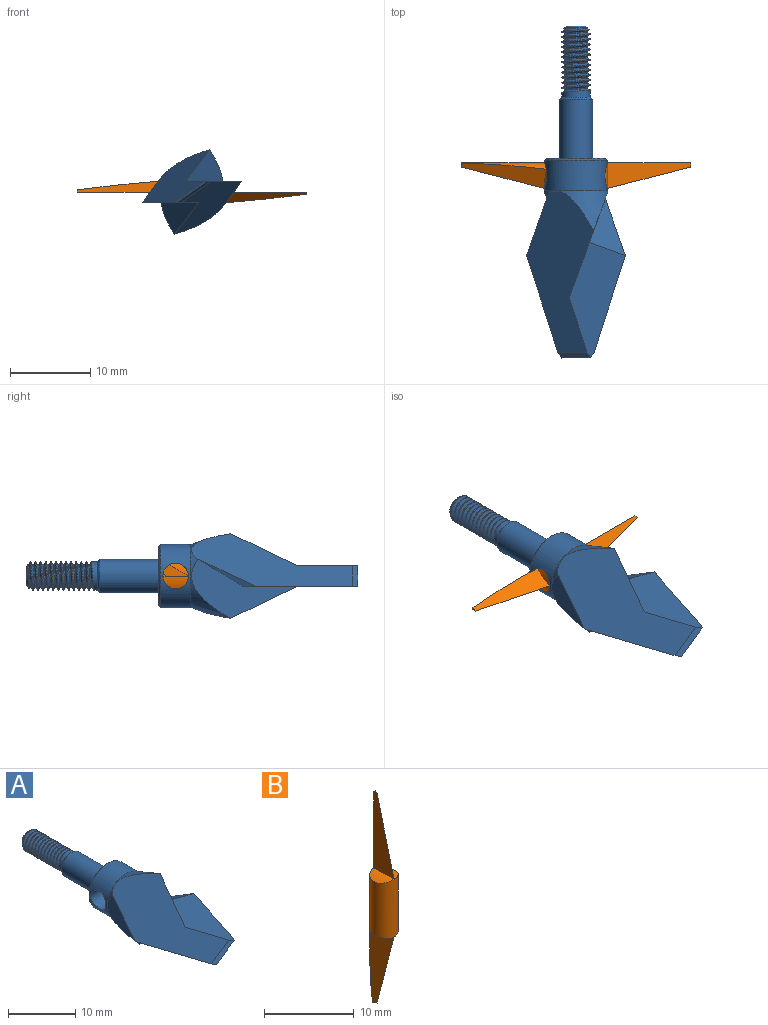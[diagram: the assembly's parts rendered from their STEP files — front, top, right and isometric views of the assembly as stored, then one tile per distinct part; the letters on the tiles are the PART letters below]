
ASSEMBLY  parts=2 mates=1
PART A: 37 faces, bbox 12.7x41.9x11.8 mm
  f0: cylinder r=2.08mm len=7.37mm, axis (0,-1,0), area 96.4mm2, adj f2,f23
  f1: plane 3.66x3.66mm, normal (0,1,0), area 0.9mm2, adj f2,f3
  f2: cone r=2.08mm half-angle=45deg, axis (0,-1,0), area 4.4mm2, adj f0,f1
  f3: cylinder r=1.75mm len=3.51mm, axis (0,-1,0), area 7.4mm2, adj f1,f4,f18,f20,f21
  f4: cylinder r=1.75mm len=3.51mm, axis (0,-1,0), area 1mm2, adj f3,f5,f20,f21
  f5: cylinder r=1.75mm len=3.51mm, axis (0,-1,0), area 1mm2, adj f4,f6,f20,f21
  f6: cylinder r=1.75mm len=3.51mm, axis (0,-1,0), area 1mm2, adj f5,f7,f20,f21
  f7: cylinder r=1.75mm len=3.51mm, axis (0,-1,0), area 1mm2, adj f6,f8,f20,f21
  f8: cylinder r=1.75mm len=3.51mm, axis (0,-1,0), area 1mm2, adj f7,f9,f20,f21
  f9: cylinder r=1.75mm len=3.51mm, axis (0,-1,0), area 1mm2, adj f8,f10,f20,f21
  f10: cylinder r=1.75mm len=3.51mm, axis (0,-1,0), area 1mm2, adj f9,f11,f20,f21
  f11: cylinder r=1.75mm len=3.51mm, axis (0,-1,0), area 1mm2, adj f10,f12,f20,f21
  f12: cylinder r=1.75mm len=3.51mm, axis (0,-1,0), area 1mm2, adj f11,f13,f20,f21
  f13: cylinder r=1.75mm len=3.51mm, axis (0,-1,0), area 1mm2, adj f12,f14,f20,f21
  f14: cylinder r=1.75mm len=3.51mm, axis (0,-1,0), area 1mm2, adj f13,f15,f20,f21
  f15: cylinder r=1.75mm len=1.33mm, axis (0,-1,0), area 0.1mm2, adj f14,f17,f20
  f16: plane 2.49x2.49mm, normal (0,1,0), area 4.9mm2, adj f17
  f17: cone r=1.24mm half-angle=45deg, axis (0,-1,0), area 4mm2, adj f15,f16,f19,f20,f21
  f18: plane 0.55x0.35mm, normal (0,0,-1), area 0.1mm2, adj f3,f19,f20,f21
  f19: cylinder r=1.4mm len=8.24mm, axis (0,1,0), area 16.6mm2, adj f17,f18,f20,f21
  f20: bspline ~8.35x4.05mm, area 49.1mm2, adj f3,f4,f5,f6,f7,f8,f9,f10
  f21: bspline ~8.46x4.05mm, area 51.4mm2, adj f3,f4,f5,f6,f7,f8,f9,f10
  f22: cylinder r=3.94mm len=7.87mm, axis (0,1,0), area 78.1mm2, adj f24,f25,f26
  f23: plane 7.37x7.37mm, normal (0,1,0), area 29mm2, adj f0,f25
  f24: cylinder r=1.59mm len=7.88mm, axis (1,0,0), area 75.2mm2, adj f22
  f25: cone r=3.94mm half-angle=45deg, axis (0,-1,0), area 8.6mm2, adj f22,f23
  f26: cone r=6.06mm half-angle=19.6deg, axis (0,-1,0), area 35mm2, adj f22,f33,f34,f35,f36
  f27: plane 4.07x2.54mm, normal (0.54,-0.34,-0.77), area 3.3mm2, adj f28,f30,f32,f36
  f28: plane 4.07x2.54mm, normal (-0.54,-0.34,0.77), area 3.3mm2, adj f27,f30,f32,f35
  f29: plane 7.11x4.5mm, normal (0.17,0.47,0.87), area 16.1mm2, adj f30,f33,f36
  f30: plane 14.4x7mm, normal (0,0,1), area 52.8mm2, adj f27,f28,f29,f33,f35,f36
  f31: plane 7.11x4.5mm, normal (-0.17,0.47,-0.87), area 16.1mm2, adj f32,f34,f35
  f32: plane 14.4x7mm, normal (0,0,-1), area 52.8mm2, adj f27,f28,f31,f34,f35,f36
  f33: plane 13.21x7.37mm, normal (0.94,-0.34,0), area 41.8mm2, adj f26,f29,f30,f35,f36
  f34: plane 13.21x7.37mm, normal (-0.94,-0.34,0), area 41.8mm2, adj f26,f31,f32,f35,f36
  f35: plane 20.05x8.35mm, normal (-0.56,-0.18,0.81), area 122.6mm2, adj f26,f28,f30,f31,f32,f33,f34
  f36: plane 20.42x8.72mm, normal (0.56,-0.18,-0.81), area 122.6mm2, adj f26,f27,f29,f30,f32,f33,f34
PART B: 11 faces, bbox 3.2x3.2x28.6 mm
  f0: cylinder r=1.59mm len=28.58mm, axis (0,0,-1), area 94.9mm2, adj f1,f2,f3,f4,f5,f6,f7,f8
  f1: plane 0.51x0.27mm, normal (0,0,-1), area 0.1mm2, adj f0,f6,f9
  f2: plane 0.51x0.27mm, normal (0,0,1), area 0.1mm2, adj f0,f4,f7
  f3: cylinder r=3.94mm len=3.18mm, axis (0,1,0), area 4mm2, adj f0,f4
  f4: plane 10.35x3.18mm, normal (-1,0,0), area 19.1mm2, adj f0,f2,f3,f7
  f5: cylinder r=3.94mm len=3.18mm, axis (0,1,0), area 4mm2, adj f0,f6
  f6: plane 10.35x3.18mm, normal (1,0,0), area 19.1mm2, adj f0,f1,f5,f9
  f7: plane 10.66x3.22mm, normal (0.87,-0.48,0.12), area 18.6mm2, adj f0,f2,f4,f8
  f8: cylinder r=3.94mm len=2.39mm, axis (0,1,0), area 1.6mm2, adj f0,f7
  f9: plane 10.67x3.22mm, normal (-0.87,-0.48,-0.12), area 18.6mm2, adj f0,f1,f6,f10
  f10: cylinder r=3.94mm len=2.39mm, axis (0,1,0), area 1.6mm2, adj f0,f9
PLACE A at identity fixed
PLACE B rot(axis=(0,1,0),90deg) t=(0,-2.16,0)mm
MATE cylindrical A.f24 <-> B.f0  axis (1,0,0) through (0,-2.16,0)mm
